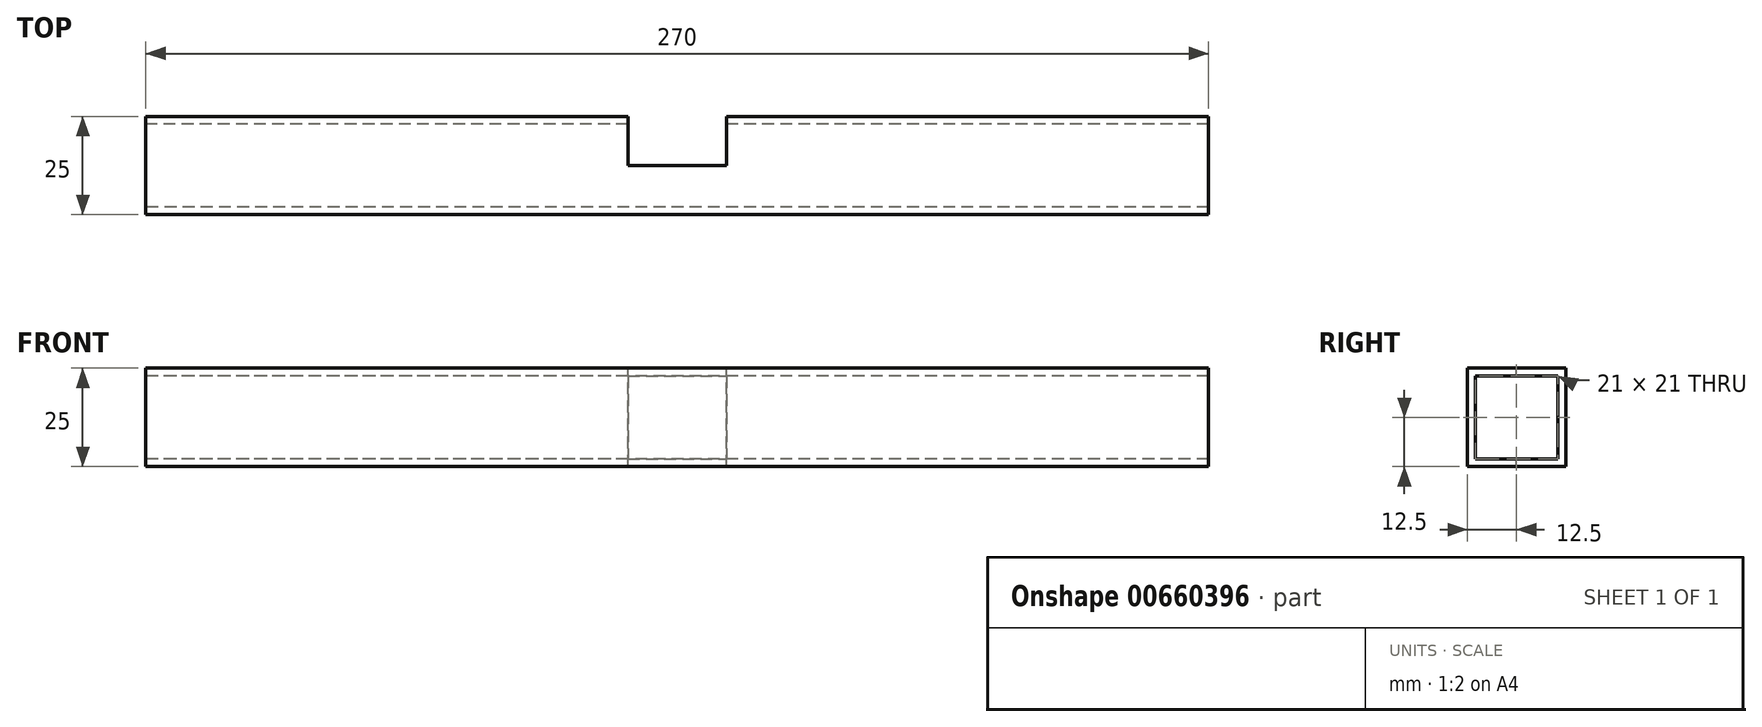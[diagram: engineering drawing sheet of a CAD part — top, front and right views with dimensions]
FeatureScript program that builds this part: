
annotation { "Feature Type Name" : "Feature", "Feature Type Description" : "" }
export const myFeature = defineFeature(function(context is Context, id is Id, definition is map)
    precondition{}
    {
        {
            var Q0;
            Q0=qCreatedBy(makeId("Right.planeOp"),FACE);
            var sketch = newSketch(context, id + "F0", { "sketchPlane" : qUnion([Q0])});
            skLineSegment(sketch, "E0.bottom", {"start": v(0, 0) * mm, "end": v(25, 0) * mm});
            skLineSegment(sketch, "E0.top", {"start": v(0, 25) * mm, "end": v(25, 25) * mm});
            skLineSegment(sketch, "E0.left", {"start": v(0, 0) * mm, "end": v(0, 25) * mm});
            skLineSegment(sketch, "E0.right", {"start": v(25, 0) * mm, "end": v(25, 25) * mm});
            skLineSegment(sketch, "E1.0", {"start": v(2, 23) * mm, "end": v(23, 23) * mm});
            skLineSegment(sketch, "E1.1", {"start": v(2, 2) * mm, "end": v(2, 23) * mm});
            skLineSegment(sketch, "E1.2", {"start": v(2, 2) * mm, "end": v(23, 2) * mm});
            skLineSegment(sketch, "E1.3", {"start": v(23, 2) * mm, "end": v(23, 23) * mm});
            skSolve(sketch);
        }
        {
            var Q0;
            Q0=makeQuery(id+"F0.imprint","IMPRINT",FACE,{"disambiguationData":[TD([[makeQuery(id+"F0.imprint","IMPRINT",EDGE,{"derivedFrom":sQuery(id+"F0.wireOp",EDGE,"E0.bottom")}),1.0]])]});
            extrude(context, id + "F1", {"entities" : qUnion([Q0]), "depth" : 270 * mm, "offsetDistance" : 25 * mm});
        }
        {
            var Q0;
            Q0=makeQuery(id+"F1.opExtrude","SWEPT_FACE",FACE,{"disambiguationData":[OSD([sQuery(id+"F0.wireOp",EDGE,"E0.top")])]});
            var sketch = newSketch(context, id + "F2", { "sketchPlane" : qUnion([Q0])});
            skLineSegment(sketch, "E2.bottom", {"start": v(122.5, 25) * mm, "end": v(147.5, 25) * mm});
            skLineSegment(sketch, "E2.top", {"start": v(122.5, 12.5) * mm, "end": v(147.5, 12.5) * mm});
            skLineSegment(sketch, "E2.left", {"start": v(122.5, 25) * mm, "end": v(122.5, 12.5) * mm});
            skLineSegment(sketch, "E2.right", {"start": v(147.5, 25) * mm, "end": v(147.5, 12.5) * mm});
            skLineSegment(sketch, "E3", {"start": v(0, 25) * mm, "end": v(122.5, 25) * mm, "construction": true});
            skLineSegment(sketch, "E4", {"start": v(147.5, 25) * mm, "end": v(270, 25) * mm, "construction": true});
            skSolve(sketch);
        }
        {
            var Q0;
            Q0=makeQuery(id+"F2.imprint","IMPRINT",FACE,{"disambiguationData":[TD([[makeQuery(id+"F2.imprint","IMPRINT",EDGE,{"derivedFrom":sQuery(id+"F2.wireOp",EDGE,"E2.bottom")}),1.0]])]});
            extrude(context, id + "F3", {"entities" : qUnion([Q0]), "operationType" : NewBodyOperationType.REMOVE, "endBound" : BoundingType.THROUGH_ALL, "oppositeDirection" : true, "depth" : 25 * mm, "offsetDistance" : 25 * mm});
        }
    });
